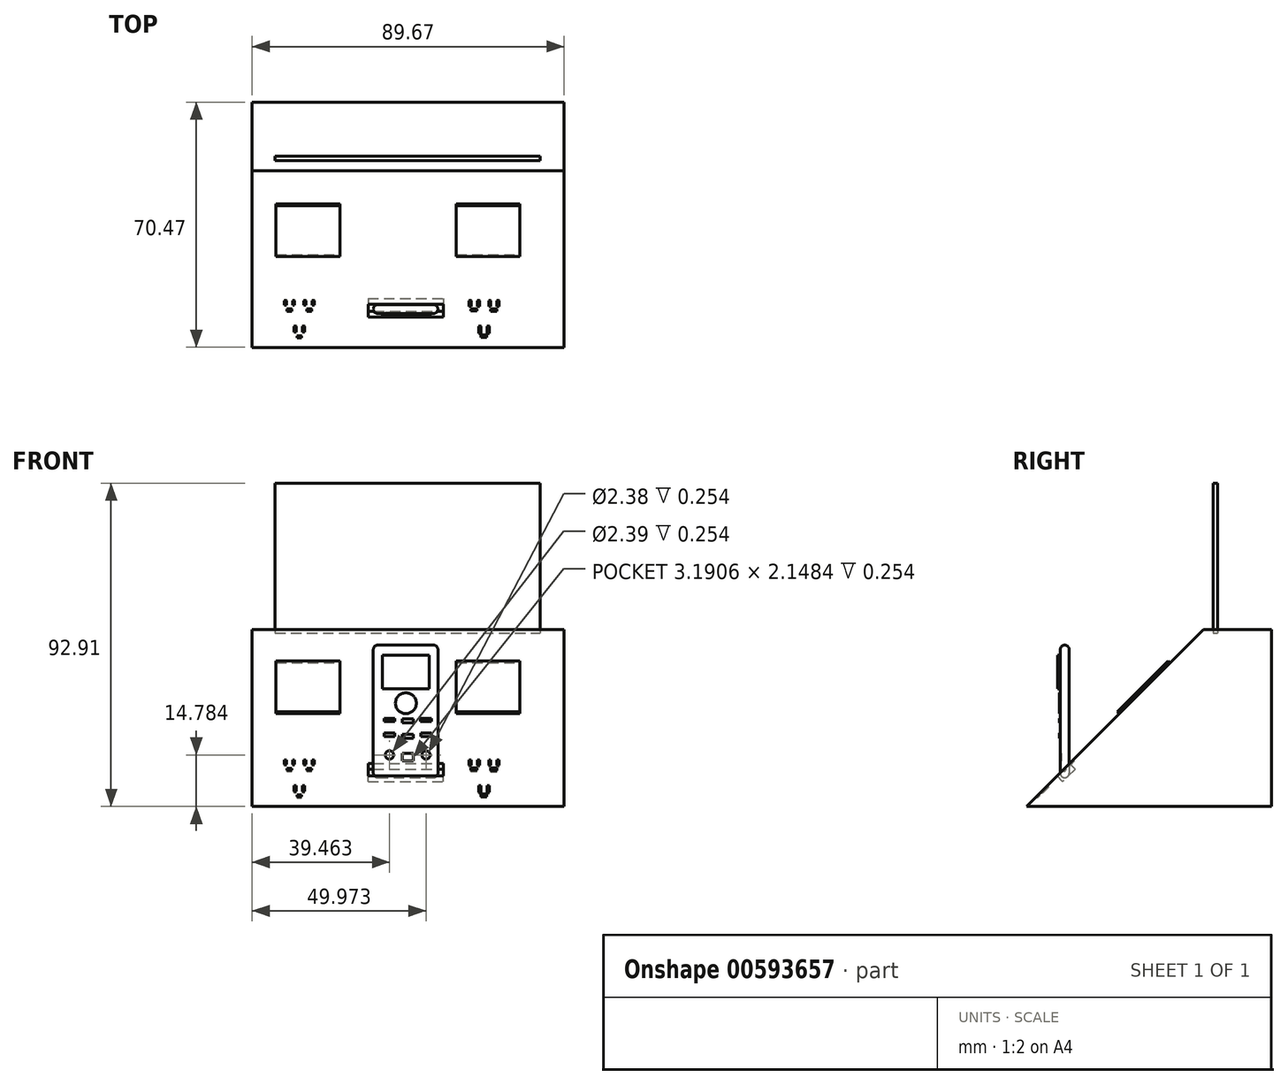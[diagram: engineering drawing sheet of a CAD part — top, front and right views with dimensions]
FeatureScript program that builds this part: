
annotation { "Feature Type Name" : "Feature", "Feature Type Description" : "" }
export const myFeature = defineFeature(function(context is Context, id is Id, definition is map)
    precondition{}
    {
        {
            var Q0;
            Q0=qCreatedBy(makeId("Top.planeOp"),FACE);
            var sketch = newSketch(context, id + "F0", { "sketchPlane" : qUnion([Q0])});
            skLineSegment(sketch, "E0.bottom", {"start": v(-44.91, 45.76) * mm, "end": v(44.76, 45.76) * mm});
            skLineSegment(sketch, "E0.top", {"start": v(-44.91, -37.41) * mm, "end": v(44.76, -37.41) * mm});
            skLineSegment(sketch, "E0.left", {"start": v(-44.91, 45.76) * mm, "end": v(-44.91, -37.41) * mm});
            skLineSegment(sketch, "E0.right", {"start": v(44.76, 45.76) * mm, "end": v(44.76, -37.41) * mm});
            skSolve(sketch);
        }
        {
            var Q0;
            Q0 = qSketchRegion(id + "F0", true);
            var Q1;
            Q1=makeQuery(id+"F0.imprint","IMPRINT",FACE,{"disambiguationData":[TD([[makeQuery(id+"F0.imprint","IMPRINT",EDGE,{"derivedFrom":sQuery(id+"F0.wireOp",EDGE,"E0.bottom")}),-1.0]])]});
            extrude(context, id + "F1", {"entities" : qUnion([Q0, Q1]), "depth" : 50.8 * mm, "offsetDistance" : 25.4 * mm});
        }
        {
            var Q0;
            Q0=makeQuery(id+"F1.opExtrude","CAP_EDGE",EDGE,{"disambiguationData":[OSD([sQuery(id+"F0.wireOp",EDGE,"E0.top")])],"isStart":false});
            chamfer(context, id + "F2", {"entities" : qUnion([Q0]), "width" : 63.5 * mm, "tangentPropagation" : true});
        }
        {
            var Q0;
            Q0=qCreatedBy(makeId("Front.planeOp"),FACE);
            var sketch = newSketch(context, id + "F3", { "sketchPlane" : qUnion([Q0])});
            skLineSegment(sketch, "E1.bottom", {"start": v(117.35, 33.47) * mm, "end": v(193.55, 33.47) * mm});
            skLineSegment(sketch, "E1.top", {"start": v(117.35, -9.66) * mm, "end": v(193.55, -9.66) * mm});
            skLineSegment(sketch, "E1.left", {"start": v(117.35, 33.47) * mm, "end": v(117.35, -9.66) * mm});
            skLineSegment(sketch, "E1.right", {"start": v(193.55, 33.47) * mm, "end": v(193.55, -9.66) * mm});
            skLineSegment(sketch, "E2.bottom", {"start": v(120.3, -7.68) * mm, "end": v(191.47, -7.68) * mm});
            skLineSegment(sketch, "E2.top", {"start": v(120.3, 31.24) * mm, "end": v(191.47, 31.24) * mm});
            skLineSegment(sketch, "E2.left", {"start": v(120.3, -7.68) * mm, "end": v(120.3, 31.24) * mm});
            skLineSegment(sketch, "E2.right", {"start": v(191.47, -7.68) * mm, "end": v(191.47, 31.24) * mm});
            skSolve(sketch);
        }
        {
            var Q0;
            Q0=makeQuery(id+"F3.imprint","IMPRINT",FACE,{"disambiguationData":[TD([[makeQuery(id+"F3.imprint","IMPRINT",EDGE,{"derivedFrom":sQuery(id+"F3.wireOp",EDGE,"E1.bottom")}),-1.0]])]});
            var Q1;
            Q1=makeQuery(id+"F3.imprint","IMPRINT",FACE,{"disambiguationData":[TD([[makeQuery(id+"F3.imprint","IMPRINT",EDGE,{"derivedFrom":sQuery(id+"F3.wireOp",EDGE,"E2.bottom")}),1.0]])]});
            extrude(context, id + "F4", {"entities" : qUnion([Q0, Q1]), "depth" : 1.27 * mm, "offsetDistance" : 25.4 * mm});
        }
        {
            var Q0;
            Q0=makeQuery(id+"F4.opExtrude","SWEPT_BODY",BODY,{"disambiguationData":[OSD([sQuery(id+"F3.wireOp",EDGE,"E1.bottom"),sQuery(id+"F3.wireOp",EDGE,"E1.top"),sQuery(id+"F3.wireOp",EDGE,"E1.left"),sQuery(id+"F3.wireOp",EDGE,"E1.right")])]});
            transform(context, id + "F5", {"entities" : qUnion([Q0]), "transformType" : TransformType.TRANSLATION_3D, "dx" : -155.7 * mm, "dy" : 30.23 * mm, "dz" : 59.44 * mm, "makeCopy" : false});
        }
        {
            var Q0;
            Q0=qCreatedBy(makeId("Front.planeOp"),FACE);
            var sketch = newSketch(context, id + "F6", { "sketchPlane" : qUnion([Q0])});
            skLineSegment(sketch, "E3.bottom", {"start": v(75.27, 43.86) * mm, "end": v(93.83, 43.86) * mm});
            skLineSegment(sketch, "E3.top", {"start": v(75.27, 5.76) * mm, "end": v(93.83, 5.76) * mm});
            skLineSegment(sketch, "E3.left", {"start": v(75.27, 43.86) * mm, "end": v(75.27, 5.76) * mm});
            skLineSegment(sketch, "E3.right", {"start": v(93.83, 43.86) * mm, "end": v(93.83, 5.76) * mm});
            skSolve(sketch);
        }
        {
            var Q0;
            Q0 = qSketchRegion(id + "F6", true);
            extrude(context, id + "F7", {"entities" : qUnion([Q0]), "depth" : 2.54 * mm, "offsetDistance" : 25.4 * mm});
        }
        {
            var Q0;
            Q0=makeQuery(id+"F7.opExtrude","CAP_EDGE",EDGE,{"disambiguationData":[OSD([sQuery(id+"F6.wireOp",EDGE,"E3.left")])],"isStart":true});
            var Q1;
            Q1=makeQuery(id+"F7.opExtrude","CAP_EDGE",EDGE,{"disambiguationData":[OSD([sQuery(id+"F6.wireOp",EDGE,"E3.left")])],"isStart":false});
            var Q2;
            Q2=makeQuery(id+"F7.opExtrude","CAP_EDGE",EDGE,{"disambiguationData":[OSD([sQuery(id+"F6.wireOp",EDGE,"E3.right")])],"isStart":true});
            var Q3;
            Q3=makeQuery(id+"F7.opExtrude","CAP_EDGE",EDGE,{"disambiguationData":[OSD([sQuery(id+"F6.wireOp",EDGE,"E3.right")])],"isStart":false});
            var Q4;
            Q4=makeQuery(id+"F7.opExtrude","SWEPT_FACE",FACE,{"disambiguationData":[OSD([sQuery(id+"F6.wireOp",EDGE,"E3.top")])]});
            var Q5;
            Q5=makeQuery(id+"F7.opExtrude","SWEPT_FACE",FACE,{"disambiguationData":[OSD([sQuery(id+"F6.wireOp",EDGE,"E3.bottom")])]});
            fillet(context, id + "F8", {"entities" : qUnion([Q0, Q1, Q2, Q3, Q4, Q5]), "radius" : 1.27 * mm, "tangentPropagation" : true, "allowEdgeOverflow" : false});
        }
        {
            var Q0;
            Q0=makeQuery(id+"F2.opChamfer","BLEND_FACE",FACE,{"disambiguationData":[OSD([sQuery(id+"F0.wireOp",EDGE,"E0.top")])]});
            var sketch = newSketch(context, id + "F9", { "sketchPlane" : qUnion([Q0])});
            skLineSegment(sketch, "E4.bottom", {"start": v(-11.58, 0) * mm, "end": v(10.01, 0) * mm});
            skLineSegment(sketch, "E4.left", {"start": v(-11.58, 0) * mm, "end": v(-11.58, 0) * mm});
            skLineSegment(sketch, "E4.right", {"start": v(10.01, 0) * mm, "end": v(10.01, 0) * mm});
            skLineSegment(sketch, "E5", {"start": v(-11.58, 0) * mm, "end": v(-11.58, -5.08) * mm});
            skLineSegment(sketch, "E6", {"start": v(-11.58, -5.08) * mm, "end": v(10.01, -5.08) * mm});
            skLineSegment(sketch, "E7", {"start": v(10.01, -5.08) * mm, "end": v(10.01, 0) * mm});
            skSolve(sketch);
        }
        {
            var Q0;
            Q0=makeQuery(id+"F9.imprint","IMPRINT",FACE,{"disambiguationData":[TD([[makeQuery(id+"F9.imprint","IMPRINT",EDGE,{"derivedFrom":sQuery(id+"F9.wireOp",EDGE,"E4.bottom")}),-1.0]])]});
            extrude(context, id + "F10", {"entities" : qUnion([Q0]), "operationType" : NewBodyOperationType.REMOVE, "oppositeDirection" : true, "depth" : 2.3 * mm, "offsetDistance" : 25.4 * mm});
        }
        {
            var Q0;
            Q0=makeQuery(id+"F7.opExtrude","SWEPT_BODY",BODY,{"disambiguationData":[OSD([sQuery(id+"F6.wireOp",EDGE,"E3.bottom"),sQuery(id+"F6.wireOp",EDGE,"E3.top"),sQuery(id+"F6.wireOp",EDGE,"E3.left"),sQuery(id+"F6.wireOp",EDGE,"E3.right")])]});
            transform(context, id + "F11", {"entities" : qUnion([Q0]), "transformType" : TransformType.TRANSLATION_3D, "dx" : -85.34 * mm, "dy" : -12.45 * mm, "dz" : 2.5 * mm, "makeCopy" : false});
        }
        {
            var Q0;
            Q0=makeQuery(id+"F7.opExtrude","CAP_FACE",FACE,{"disambiguationData":[OSD([sQuery(id+"F6.wireOp",EDGE,"E3.bottom"),sQuery(id+"F6.wireOp",EDGE,"E3.top"),sQuery(id+"F6.wireOp",EDGE,"E3.left"),sQuery(id+"F6.wireOp",EDGE,"E3.right")])],"isStart":false});
            var sketch = newSketch(context, id + "F12", { "sketchPlane" : qUnion([Q0])});
            skLineSegment(sketch, "E8.bottom", {"start": v(-7.42, 43.5) * mm, "end": v(5.98, 43.5) * mm});
            skLineSegment(sketch, "E8.top", {"start": v(-7.42, 33.79) * mm, "end": v(5.98, 33.79) * mm});
            skLineSegment(sketch, "E8.left", {"start": v(-7.42, 43.5) * mm, "end": v(-7.42, 33.79) * mm});
            skLineSegment(sketch, "E8.right", {"start": v(5.98, 43.5) * mm, "end": v(5.98, 33.79) * mm});
            skSolve(sketch);
        }
        {
            var Q0;
            Q0=makeQuery(id+"F12.imprint","IMPRINT",FACE,{"disambiguationData":[TD([[makeQuery(id+"F12.imprint","IMPRINT",EDGE,{"derivedFrom":sQuery(id+"F12.wireOp",EDGE,"E8.bottom")}),-1.0]])]});
            var Q1;
            Q1 = qSketchRegion(id + "F14", true);
            extrude(context, id + "F13", {"entities" : qUnion([Q0, Q1]), "operationType" : NewBodyOperationType.ADD, "depth" : 0.76 * mm, "offsetDistance" : 25.4 * mm});
        }
        {
            var Q0;
            Q0=makeQuery(id+"F7.opExtrude","CAP_FACE",FACE,{"disambiguationData":[OSD([sQuery(id+"F6.wireOp",EDGE,"E3.bottom"),sQuery(id+"F6.wireOp",EDGE,"E3.top"),sQuery(id+"F6.wireOp",EDGE,"E3.left"),sQuery(id+"F6.wireOp",EDGE,"E3.right")])],"isStart":false});
            var sketch = newSketch(context, id + "F14", { "sketchPlane" : qUnion([Q0])});
            skCircle(sketch, "E9", {"center": v(-0.72, 29.65) * mm, "radius": 3 * mm});
            skPoint(sketch, "E9.centerSnap0", {"position": v(-0.72, 33.79) * mm});
            skLineSegment(sketch, "E10.bottom", {"start": v(-7.02, 25.3) * mm, "end": v(-3.87, 25.3) * mm});
            skLineSegment(sketch, "E10.top", {"start": v(-7.02, 24.42) * mm, "end": v(-3.87, 24.42) * mm});
            skLineSegment(sketch, "E10.left", {"start": v(-7.02, 25.3) * mm, "end": v(-7.02, 24.42) * mm});
            skLineSegment(sketch, "E10.right", {"start": v(-3.87, 25.3) * mm, "end": v(-3.87, 24.42) * mm});
            skLineSegment(sketch, "E11.bottom", {"start": v(-1.77, 25.15) * mm, "end": v(1.39, 25.15) * mm});
            skLineSegment(sketch, "E11.top", {"start": v(-1.77, 23.99) * mm, "end": v(1.39, 23.99) * mm});
            skLineSegment(sketch, "E11.left", {"start": v(-1.77, 25.15) * mm, "end": v(-1.77, 23.99) * mm});
            skLineSegment(sketch, "E11.right", {"start": v(1.39, 25.15) * mm, "end": v(1.39, 23.99) * mm});
            skLineSegment(sketch, "E12.bottom", {"start": v(3.5, 25.3) * mm, "end": v(6.64, 25.3) * mm});
            skLineSegment(sketch, "E12.top", {"start": v(3.5, 24.42) * mm, "end": v(6.64, 24.42) * mm});
            skLineSegment(sketch, "E12.left", {"start": v(3.5, 25.3) * mm, "end": v(3.5, 24.42) * mm});
            skLineSegment(sketch, "E12.right", {"start": v(6.64, 25.3) * mm, "end": v(6.64, 24.42) * mm});
            skLineSegment(sketch, "E13.bottom", {"start": v(-7.02, 21.07) * mm, "end": v(-3.87, 21.07) * mm});
            skLineSegment(sketch, "E13.top", {"start": v(-7.02, 20.14) * mm, "end": v(-3.87, 20.14) * mm});
            skLineSegment(sketch, "E13.left", {"start": v(-7.02, 21.07) * mm, "end": v(-7.02, 20.14) * mm});
            skLineSegment(sketch, "E13.right", {"start": v(-3.87, 21.07) * mm, "end": v(-3.87, 20.14) * mm});
            skLineSegment(sketch, "E14.bottom", {"start": v(-1.77, 20.68) * mm, "end": v(1.39, 20.68) * mm});
            skLineSegment(sketch, "E14.top", {"start": v(-1.77, 19.54) * mm, "end": v(1.39, 19.54) * mm});
            skLineSegment(sketch, "E14.left", {"start": v(-1.77, 20.68) * mm, "end": v(-1.77, 19.54) * mm});
            skLineSegment(sketch, "E14.right", {"start": v(1.39, 20.68) * mm, "end": v(1.39, 19.54) * mm});
            skLineSegment(sketch, "E15.bottom", {"start": v(3.55, 21.07) * mm, "end": v(6.58, 21.07) * mm});
            skLineSegment(sketch, "E15.top", {"start": v(3.55, 20.14) * mm, "end": v(6.58, 20.14) * mm});
            skLineSegment(sketch, "E15.left", {"start": v(3.55, 21.07) * mm, "end": v(3.55, 20.14) * mm});
            skLineSegment(sketch, "E15.right", {"start": v(6.58, 21.07) * mm, "end": v(6.58, 20.14) * mm});
            skCircle(sketch, "E16", {"center": v(-5.45, 14.78) * mm, "radius": 1.2 * mm});
            skPoint(sketch, "E16.centerSnap0", {"position": v(-5.45, 20.14) * mm});
            skCircle(sketch, "E17", {"center": v(5.06, 14.78) * mm, "radius": 1.2 * mm});
            skPoint(sketch, "E17.centerSnap0", {"position": v(5.06, 20.14) * mm});
            skPoint(sketch, "E18.centerSnap0", {"position": v(-0.2, 19.54) * mm});
            skLineSegment(sketch, "E19.bottom", {"start": v(-1.77, 15.22) * mm, "end": v(1.42, 15.22) * mm});
            skLineSegment(sketch, "E19.top", {"start": v(-1.77, 13.07) * mm, "end": v(1.42, 13.07) * mm});
            skLineSegment(sketch, "E19.left", {"start": v(-1.77, 15.22) * mm, "end": v(-1.77, 13.07) * mm});
            skLineSegment(sketch, "E19.right", {"start": v(1.42, 15.22) * mm, "end": v(1.42, 13.07) * mm});
            skSolve(sketch);
        }
        {
            var Q0;
            Q0=makeQuery(id+"F14.imprint","IMPRINT",FACE,{"disambiguationData":[TD([[makeQuery(id+"F14.imprint","IMPRINT",EDGE,{"derivedFrom":sQuery(id+"F14.wireOp",EDGE,"E9")}),1.0]])]});
            var Q1;
            Q1=makeQuery(id+"F14.imprint","IMPRINT",FACE,{"disambiguationData":[TD([[makeQuery(id+"F14.imprint","IMPRINT",EDGE,{"derivedFrom":sQuery(id+"F14.wireOp",EDGE,"E10.bottom")}),-1.0]])]});
            var Q2;
            Q2=makeQuery(id+"F14.imprint","IMPRINT",FACE,{"disambiguationData":[TD([[makeQuery(id+"F14.imprint","IMPRINT",EDGE,{"derivedFrom":sQuery(id+"F14.wireOp",EDGE,"E11.bottom")}),-1.0]])]});
            var Q3;
            Q3=makeQuery(id+"F14.imprint","IMPRINT",FACE,{"disambiguationData":[TD([[makeQuery(id+"F14.imprint","IMPRINT",EDGE,{"derivedFrom":sQuery(id+"F14.wireOp",EDGE,"E12.bottom")}),-1.0]])]});
            var Q4;
            Q4=makeQuery(id+"F14.imprint","IMPRINT",FACE,{"disambiguationData":[TD([[makeQuery(id+"F14.imprint","IMPRINT",EDGE,{"derivedFrom":sQuery(id+"F14.wireOp",EDGE,"E13.bottom")}),-1.0]])]});
            var Q5;
            Q5=makeQuery(id+"F14.imprint","IMPRINT",FACE,{"disambiguationData":[TD([[makeQuery(id+"F14.imprint","IMPRINT",EDGE,{"derivedFrom":sQuery(id+"F14.wireOp",EDGE,"E14.bottom")}),-1.0]])]});
            var Q6;
            Q6=makeQuery(id+"F14.imprint","IMPRINT",FACE,{"disambiguationData":[TD([[makeQuery(id+"F14.imprint","IMPRINT",EDGE,{"derivedFrom":sQuery(id+"F14.wireOp",EDGE,"E15.bottom")}),-1.0]])]});
            extrude(context, id + "F15", {"entities" : qUnion([Q0, Q1, Q2, Q3, Q4, Q5, Q6]), "operationType" : NewBodyOperationType.ADD, "depth" : 0.25 * mm, "offsetDistance" : 25.4 * mm});
        }
        {
            var Q0;
            Q0=makeQuery(id+"F14.imprint","IMPRINT",FACE,{"disambiguationData":[TD([[makeQuery(id+"F14.imprint","IMPRINT",EDGE,{"derivedFrom":sQuery(id+"F14.wireOp",EDGE,"E16")}),1.0]])]});
            var Q1;
            Q1=makeQuery(id+"F14.imprint","IMPRINT",FACE,{"disambiguationData":[TD([[makeQuery(id+"F14.imprint","IMPRINT",EDGE,{"derivedFrom":sQuery(id+"F14.wireOp",EDGE,"E18")}),1.0]])]});
            var Q2;
            Q2=makeQuery(id+"F14.imprint","IMPRINT",FACE,{"disambiguationData":[TD([[makeQuery(id+"F14.imprint","IMPRINT",EDGE,{"derivedFrom":sQuery(id+"F14.wireOp",EDGE,"E17")}),1.0]])]});
            var Q3;
            Q3=makeQuery(id+"F14.imprint","IMPRINT",FACE,{"disambiguationData":[TD([[makeQuery(id+"F14.imprint","IMPRINT",EDGE,{"derivedFrom":sQuery(id+"F14.wireOp",EDGE,"E19.bottom")}),-1.0]])]});
            extrude(context, id + "F16", {"entities" : qUnion([Q0, Q1, Q2, Q3]), "operationType" : NewBodyOperationType.REMOVE, "oppositeDirection" : true, "depth" : 0.25 * mm, "offsetDistance" : 25.4 * mm});
        }
        {
            var Q0;
            Q0=makeQuery(id+"F2.opChamfer","BLEND_FACE",FACE,{"disambiguationData":[OSD([sQuery(id+"F0.wireOp",EDGE,"E0.top")])]});
            var sketch = newSketch(context, id + "F17", { "sketchPlane" : qUnion([Q0])});
            skLineSegment(sketch, "E20.bottom", {"start": v(-38.07, 40.86) * mm, "end": v(-19.71, 40.86) * mm});
            skLineSegment(sketch, "E20.top", {"start": v(-38.07, 20.24) * mm, "end": v(-19.71, 20.24) * mm});
            skLineSegment(sketch, "E20.left", {"start": v(-38.07, 40.86) * mm, "end": v(-38.07, 20.24) * mm});
            skLineSegment(sketch, "E20.right", {"start": v(-19.71, 40.86) * mm, "end": v(-19.71, 20.24) * mm});
            skLineSegment(sketch, "E21.bottom", {"start": v(13.74, 40.86) * mm, "end": v(32.09, 40.86) * mm});
            skLineSegment(sketch, "E21.top", {"start": v(13.74, 20.24) * mm, "end": v(32.09, 20.24) * mm});
            skLineSegment(sketch, "E21.left", {"start": v(13.74, 40.86) * mm, "end": v(13.74, 20.24) * mm});
            skLineSegment(sketch, "E21.right", {"start": v(32.09, 40.86) * mm, "end": v(32.09, 20.24) * mm});
            skSolve(sketch);
        }
        {
            var Q0;
            Q0=makeQuery(id+"F17.imprint","IMPRINT",FACE,{"disambiguationData":[TD([[makeQuery(id+"F17.imprint","IMPRINT",EDGE,{"derivedFrom":sQuery(id+"F17.wireOp",EDGE,"E20.bottom")}),-1.0]])]});
            var Q1;
            Q1=makeQuery(id+"F17.imprint","IMPRINT",FACE,{"disambiguationData":[TD([[makeQuery(id+"F17.imprint","IMPRINT",EDGE,{"derivedFrom":sQuery(id+"F17.wireOp",EDGE,"E21.bottom")}),-1.0]])]});
            extrude(context, id + "F18", {"entities" : qUnion([Q0, Q1]), "operationType" : NewBodyOperationType.ADD, "depth" : 0.76 * mm, "offsetDistance" : 25.4 * mm});
        }
        {
            var Q0;
            Q0=makeQuery(id+"F2.opChamfer","BLEND_FACE",FACE,{"disambiguationData":[OSD([sQuery(id+"F0.wireOp",EDGE,"E0.top")])]});
            var sketch = newSketch(context, id + "F19", { "sketchPlane" : qUnion([Q0])});
            skLineSegment(sketch, "E22.bottom", {"start": v(-36.96, 2.3) * mm, "end": v(-31.3, 2.3) * mm});
            skLineSegment(sketch, "E22.top", {"start": v(-36.96, -3.9) * mm, "end": v(-31.3, -3.9) * mm});
            skLineSegment(sketch, "E22.left", {"start": v(-36.96, 2.3) * mm, "end": v(-36.96, -3.9) * mm});
            skLineSegment(sketch, "E22.right", {"start": v(-31.3, 2.3) * mm, "end": v(-31.3, -3.9) * mm});
            skLineSegment(sketch, "E23.bottom", {"start": v(-31.3, 2.3) * mm, "end": v(-25.63, 2.3) * mm});
            skLineSegment(sketch, "E23.top", {"start": v(-31.3, -3.9) * mm, "end": v(-25.63, -3.9) * mm});
            skLineSegment(sketch, "E23.right", {"start": v(-25.63, 2.3) * mm, "end": v(-25.63, -3.9) * mm});
            skPoint(sketch, "E24.firstSnap0", {"position": v(-34.12, -3.9) * mm});
            skPoint(sketch, "E24.oppositeSnap0", {"position": v(-28.46, -3.9) * mm});
            skLineSegment(sketch, "E24.bottom", {"start": v(-34.12, -7.4) * mm, "end": v(-28.46, -7.4) * mm});
            skLineSegment(sketch, "E24.top", {"start": v(-34.12, -14.4) * mm, "end": v(-28.46, -14.4) * mm});
            skLineSegment(sketch, "E24.left", {"start": v(-34.12, -7.4) * mm, "end": v(-34.12, -14.4) * mm});
            skLineSegment(sketch, "E24.right", {"start": v(-28.46, -7.4) * mm, "end": v(-28.46, -14.4) * mm});
            skLineSegment(sketch, "E25.bottom", {"start": v(16.14, 2.3) * mm, "end": v(21.8, 2.3) * mm});
            skLineSegment(sketch, "E25.top", {"start": v(16.14, -3.9) * mm, "end": v(21.8, -3.9) * mm});
            skLineSegment(sketch, "E25.left", {"start": v(16.14, 2.3) * mm, "end": v(16.14, -3.9) * mm});
            skLineSegment(sketch, "E25.right", {"start": v(21.8, 2.3) * mm, "end": v(21.8, -3.9) * mm});
            skLineSegment(sketch, "E26.bottom", {"start": v(21.8, 2.3) * mm, "end": v(27.46, 2.3) * mm});
            skLineSegment(sketch, "E26.top", {"start": v(21.8, -3.9) * mm, "end": v(27.46, -3.9) * mm});
            skLineSegment(sketch, "E26.right", {"start": v(27.46, 2.3) * mm, "end": v(27.46, -3.9) * mm});
            skPoint(sketch, "E27.firstSnap0", {"position": v(18.97, -3.9) * mm});
            skPoint(sketch, "E27.oppositeSnap0", {"position": v(24.63, -3.9) * mm});
            skLineSegment(sketch, "E27.bottom", {"start": v(18.97, -7.74) * mm, "end": v(24.63, -7.74) * mm});
            skLineSegment(sketch, "E27.top", {"start": v(18.97, -14.4) * mm, "end": v(24.63, -14.4) * mm});
            skLineSegment(sketch, "E27.left", {"start": v(18.97, -7.74) * mm, "end": v(18.97, -14.4) * mm});
            skLineSegment(sketch, "E27.right", {"start": v(24.63, -7.74) * mm, "end": v(24.63, -14.4) * mm});
            skLineSegment(sketch, "E28.bottom", {"start": v(-35.69, 1.48) * mm, "end": v(-35.06, 1.48) * mm});
            skLineSegment(sketch, "E28.top", {"start": v(-35.69, -0.36) * mm, "end": v(-35.06, -0.36) * mm});
            skLineSegment(sketch, "E28.left", {"start": v(-35.69, 1.48) * mm, "end": v(-35.69, -0.36) * mm});
            skLineSegment(sketch, "E28.right", {"start": v(-35.06, 1.48) * mm, "end": v(-35.06, -0.36) * mm});
            skLineSegment(sketch, "E29.bottom", {"start": v(-33.31, 1.48) * mm, "end": v(-32.75, 1.48) * mm});
            skLineSegment(sketch, "E29.top", {"start": v(-33.31, -0.36) * mm, "end": v(-32.75, -0.36) * mm});
            skLineSegment(sketch, "E29.left", {"start": v(-33.31, 1.48) * mm, "end": v(-33.31, -0.36) * mm});
            skLineSegment(sketch, "E29.right", {"start": v(-32.75, 1.48) * mm, "end": v(-32.75, -0.36) * mm});
            skLineSegment(sketch, "E30.bottom", {"start": v(-30.02, 1.48) * mm, "end": v(-29.39, 1.48) * mm});
            skLineSegment(sketch, "E30.top", {"start": v(-30.02, -0.36) * mm, "end": v(-29.39, -0.36) * mm});
            skLineSegment(sketch, "E30.left", {"start": v(-30.02, 1.48) * mm, "end": v(-30.02, -0.36) * mm});
            skLineSegment(sketch, "E30.right", {"start": v(-29.39, 1.48) * mm, "end": v(-29.39, -0.36) * mm});
            skLineSegment(sketch, "E31.bottom", {"start": v(-27.63, 1.48) * mm, "end": v(-27, 1.48) * mm});
            skLineSegment(sketch, "E31.top", {"start": v(-27.63, -0.36) * mm, "end": v(-27, -0.36) * mm});
            skLineSegment(sketch, "E31.left", {"start": v(-27.63, 1.48) * mm, "end": v(-27.63, -0.36) * mm});
            skLineSegment(sketch, "E31.right", {"start": v(-27, 1.48) * mm, "end": v(-27, -0.36) * mm});
            skLineSegment(sketch, "E32.bottom", {"start": v(-32.85, -8.98) * mm, "end": v(-32.22, -8.98) * mm});
            skLineSegment(sketch, "E32.top", {"start": v(-32.85, -11.3) * mm, "end": v(-32.22, -11.3) * mm});
            skLineSegment(sketch, "E32.left", {"start": v(-32.85, -8.98) * mm, "end": v(-32.85, -11.3) * mm});
            skLineSegment(sketch, "E32.right", {"start": v(-32.22, -8.98) * mm, "end": v(-32.22, -11.3) * mm});
            skLineSegment(sketch, "E33.bottom", {"start": v(-30.47, -8.98) * mm, "end": v(-29.83, -8.98) * mm});
            skLineSegment(sketch, "E33.top", {"start": v(-30.47, -11.3) * mm, "end": v(-29.83, -11.3) * mm});
            skLineSegment(sketch, "E33.left", {"start": v(-30.47, -8.98) * mm, "end": v(-30.47, -11.3) * mm});
            skLineSegment(sketch, "E33.right", {"start": v(-29.83, -8.98) * mm, "end": v(-29.83, -11.3) * mm});
            skLineSegment(sketch, "E34.bottom", {"start": v(-34.88, -1.96) * mm, "end": v(-33.52, -1.96) * mm});
            skLineSegment(sketch, "E34.top", {"start": v(-34.88, -2.77) * mm, "end": v(-33.52, -2.77) * mm});
            skLineSegment(sketch, "E34.left", {"start": v(-34.88, -1.96) * mm, "end": v(-34.88, -2.77) * mm});
            skLineSegment(sketch, "E34.right", {"start": v(-33.52, -1.96) * mm, "end": v(-33.52, -2.77) * mm});
            skLineSegment(sketch, "E35.bottom", {"start": v(-29.15, -1.96) * mm, "end": v(-27.84, -1.96) * mm});
            skLineSegment(sketch, "E35.top", {"start": v(-29.15, -2.77) * mm, "end": v(-27.84, -2.77) * mm});
            skLineSegment(sketch, "E35.left", {"start": v(-29.15, -1.96) * mm, "end": v(-29.15, -2.77) * mm});
            skLineSegment(sketch, "E35.right", {"start": v(-27.84, -1.96) * mm, "end": v(-27.84, -2.77) * mm});
            skLineSegment(sketch, "E36.bottom", {"start": v(-32.03, -12.85) * mm, "end": v(-30.67, -12.85) * mm});
            skLineSegment(sketch, "E36.top", {"start": v(-32.03, -13.54) * mm, "end": v(-30.67, -13.54) * mm});
            skLineSegment(sketch, "E36.left", {"start": v(-32.03, -12.85) * mm, "end": v(-32.03, -13.54) * mm});
            skLineSegment(sketch, "E36.right", {"start": v(-30.67, -12.85) * mm, "end": v(-30.67, -13.54) * mm});
            skPoint(sketch, "E37.oppositeSnap0", {"position": v(16.14, -0.8) * mm});
            skLineSegment(sketch, "E37.bottom", {"start": v(17.4, 1.48) * mm, "end": v(18.04, 1.48) * mm});
            skLineSegment(sketch, "E37.top", {"start": v(17.4, -0.8) * mm, "end": v(18.04, -0.8) * mm});
            skLineSegment(sketch, "E37.left", {"start": v(17.4, 1.48) * mm, "end": v(17.4, -0.8) * mm});
            skLineSegment(sketch, "E37.right", {"start": v(18.04, 1.48) * mm, "end": v(18.04, -0.8) * mm});
            skLineSegment(sketch, "E38.bottom", {"start": v(19.8, 1.48) * mm, "end": v(20.43, 1.48) * mm});
            skLineSegment(sketch, "E38.top", {"start": v(19.8, -0.8) * mm, "end": v(20.43, -0.8) * mm});
            skLineSegment(sketch, "E38.left", {"start": v(19.8, 1.48) * mm, "end": v(19.8, -0.8) * mm});
            skLineSegment(sketch, "E38.right", {"start": v(20.43, 1.48) * mm, "end": v(20.43, -0.8) * mm});
            skLineSegment(sketch, "E39.bottom", {"start": v(23.07, 1.48) * mm, "end": v(23.7, 1.48) * mm});
            skLineSegment(sketch, "E39.top", {"start": v(23.07, -0.8) * mm, "end": v(23.7, -0.8) * mm});
            skLineSegment(sketch, "E39.left", {"start": v(23.07, 1.48) * mm, "end": v(23.07, -0.8) * mm});
            skLineSegment(sketch, "E39.right", {"start": v(23.7, 1.48) * mm, "end": v(23.7, -0.8) * mm});
            skLineSegment(sketch, "E40.bottom", {"start": v(25.46, 1.48) * mm, "end": v(26.1, 1.48) * mm});
            skLineSegment(sketch, "E40.top", {"start": v(25.46, -0.8) * mm, "end": v(26.1, -0.8) * mm});
            skLineSegment(sketch, "E40.left", {"start": v(25.46, 1.48) * mm, "end": v(25.46, -0.8) * mm});
            skLineSegment(sketch, "E40.right", {"start": v(26.1, 1.48) * mm, "end": v(26.1, -0.8) * mm});
            skLineSegment(sketch, "E41.bottom", {"start": v(22.62, -8.98) * mm, "end": v(23.26, -8.98) * mm});
            skLineSegment(sketch, "E41.top", {"start": v(22.62, -11.74) * mm, "end": v(23.26, -11.74) * mm});
            skLineSegment(sketch, "E41.left", {"start": v(22.62, -8.98) * mm, "end": v(22.62, -11.74) * mm});
            skLineSegment(sketch, "E41.right", {"start": v(23.26, -8.98) * mm, "end": v(23.26, -11.74) * mm});
            skLineSegment(sketch, "E42.bottom", {"start": v(20.24, -8.98) * mm, "end": v(20.87, -8.98) * mm});
            skLineSegment(sketch, "E42.top", {"start": v(20.24, -11.74) * mm, "end": v(20.87, -11.74) * mm});
            skLineSegment(sketch, "E42.left", {"start": v(20.24, -8.98) * mm, "end": v(20.24, -11.74) * mm});
            skLineSegment(sketch, "E42.right", {"start": v(20.87, -8.98) * mm, "end": v(20.87, -11.74) * mm});
            skLineSegment(sketch, "E43.bottom", {"start": v(17.97, -1.87) * mm, "end": v(19.74, -1.87) * mm});
            skLineSegment(sketch, "E43.top", {"start": v(17.97, -2.73) * mm, "end": v(19.74, -2.73) * mm});
            skLineSegment(sketch, "E43.left", {"start": v(17.97, -1.87) * mm, "end": v(17.97, -2.73) * mm});
            skLineSegment(sketch, "E43.right", {"start": v(19.74, -1.87) * mm, "end": v(19.74, -2.73) * mm});
            skLineSegment(sketch, "E44.bottom", {"start": v(23.7, -1.9) * mm, "end": v(25.44, -1.9) * mm});
            skLineSegment(sketch, "E44.top", {"start": v(23.7, -2.88) * mm, "end": v(25.44, -2.88) * mm});
            skLineSegment(sketch, "E44.left", {"start": v(23.7, -1.9) * mm, "end": v(23.7, -2.88) * mm});
            skLineSegment(sketch, "E44.right", {"start": v(25.44, -1.9) * mm, "end": v(25.44, -2.88) * mm});
            skLineSegment(sketch, "E45.bottom", {"start": v(20.86, -12.47) * mm, "end": v(22.5, -12.47) * mm});
            skLineSegment(sketch, "E45.top", {"start": v(20.86, -13.42) * mm, "end": v(22.5, -13.42) * mm});
            skLineSegment(sketch, "E45.left", {"start": v(20.86, -12.47) * mm, "end": v(20.86, -13.42) * mm});
            skLineSegment(sketch, "E45.right", {"start": v(22.5, -12.47) * mm, "end": v(22.5, -13.42) * mm});
            skSolve(sketch);
        }
        {
            var Q0;
            Q0=makeQuery(id+"F19.imprint","IMPRINT",FACE,{"disambiguationData":[TD([[makeQuery(id+"F19.imprint","IMPRINT",EDGE,{"derivedFrom":sQuery(id+"F19.wireOp",EDGE,"E28.bottom")}),-1.0]])]});
            var Q1;
            Q1=makeQuery(id+"F19.imprint","IMPRINT",FACE,{"disambiguationData":[TD([[makeQuery(id+"F19.imprint","IMPRINT",EDGE,{"derivedFrom":sQuery(id+"F19.wireOp",EDGE,"E34.bottom")}),-1.0]])]});
            var Q2;
            Q2=makeQuery(id+"F19.imprint","IMPRINT",FACE,{"disambiguationData":[TD([[makeQuery(id+"F19.imprint","IMPRINT",EDGE,{"derivedFrom":sQuery(id+"F19.wireOp",EDGE,"E29.bottom")}),-1.0]])]});
            var Q3;
            Q3=makeQuery(id+"F19.imprint","IMPRINT",FACE,{"disambiguationData":[TD([[makeQuery(id+"F19.imprint","IMPRINT",EDGE,{"derivedFrom":sQuery(id+"F19.wireOp",EDGE,"E30.bottom")}),-1.0]])]});
            var Q4;
            Q4=makeQuery(id+"F19.imprint","IMPRINT",FACE,{"disambiguationData":[TD([[makeQuery(id+"F19.imprint","IMPRINT",EDGE,{"derivedFrom":sQuery(id+"F19.wireOp",EDGE,"E35.bottom")}),-1.0]])]});
            var Q5;
            Q5=makeQuery(id+"F19.imprint","IMPRINT",FACE,{"disambiguationData":[TD([[makeQuery(id+"F19.imprint","IMPRINT",EDGE,{"derivedFrom":sQuery(id+"F19.wireOp",EDGE,"E31.bottom")}),-1.0]])]});
            var Q6;
            Q6=makeQuery(id+"F19.imprint","IMPRINT",FACE,{"disambiguationData":[TD([[makeQuery(id+"F19.imprint","IMPRINT",EDGE,{"derivedFrom":sQuery(id+"F19.wireOp",EDGE,"E32.bottom")}),-1.0]])]});
            var Q7;
            Q7=makeQuery(id+"F19.imprint","IMPRINT",FACE,{"disambiguationData":[TD([[makeQuery(id+"F19.imprint","IMPRINT",EDGE,{"derivedFrom":sQuery(id+"F19.wireOp",EDGE,"E33.bottom")}),-1.0]])]});
            var Q8;
            Q8=makeQuery(id+"F19.imprint","IMPRINT",FACE,{"disambiguationData":[TD([[makeQuery(id+"F19.imprint","IMPRINT",EDGE,{"derivedFrom":sQuery(id+"F19.wireOp",EDGE,"E36.bottom")}),-1.0]])]});
            var Q9;
            Q9=makeQuery(id+"F19.imprint","IMPRINT",FACE,{"disambiguationData":[TD([[makeQuery(id+"F19.imprint","IMPRINT",EDGE,{"derivedFrom":sQuery(id+"F19.wireOp",EDGE,"E43.bottom")}),-1.0]])]});
            var Q10;
            Q10=makeQuery(id+"F19.imprint","IMPRINT",FACE,{"disambiguationData":[TD([[makeQuery(id+"F19.imprint","IMPRINT",EDGE,{"derivedFrom":sQuery(id+"F19.wireOp",EDGE,"E44.bottom")}),-1.0]])]});
            var Q11;
            Q11=makeQuery(id+"F19.imprint","IMPRINT",FACE,{"disambiguationData":[TD([[makeQuery(id+"F19.imprint","IMPRINT",EDGE,{"derivedFrom":sQuery(id+"F19.wireOp",EDGE,"E45.bottom")}),-1.0]])]});
            var Q12;
            Q12=makeQuery(id+"F19.imprint","IMPRINT",FACE,{"disambiguationData":[TD([[makeQuery(id+"F19.imprint","IMPRINT",EDGE,{"derivedFrom":sQuery(id+"F19.wireOp",EDGE,"E42.bottom")}),-1.0]])]});
            var Q13;
            Q13=makeQuery(id+"F19.imprint","IMPRINT",FACE,{"disambiguationData":[TD([[makeQuery(id+"F19.imprint","IMPRINT",EDGE,{"derivedFrom":sQuery(id+"F19.wireOp",EDGE,"E39.bottom")}),-1.0]])]});
            var Q14;
            Q14=makeQuery(id+"F19.imprint","IMPRINT",FACE,{"disambiguationData":[TD([[makeQuery(id+"F19.imprint","IMPRINT",EDGE,{"derivedFrom":sQuery(id+"F19.wireOp",EDGE,"E40.bottom")}),-1.0]])]});
            var Q15;
            Q15=makeQuery(id+"F19.imprint","IMPRINT",FACE,{"disambiguationData":[TD([[makeQuery(id+"F19.imprint","IMPRINT",EDGE,{"derivedFrom":sQuery(id+"F19.wireOp",EDGE,"E38.bottom")}),-1.0]])]});
            var Q16;
            Q16=makeQuery(id+"F19.imprint","IMPRINT",FACE,{"disambiguationData":[TD([[makeQuery(id+"F19.imprint","IMPRINT",EDGE,{"derivedFrom":sQuery(id+"F19.wireOp",EDGE,"E37.bottom")}),-1.0]])]});
            var Q17;
            Q17=makeQuery(id+"F19.imprint","IMPRINT",FACE,{"disambiguationData":[TD([[makeQuery(id+"F19.imprint","IMPRINT",EDGE,{"derivedFrom":sQuery(id+"F19.wireOp",EDGE,"E41.bottom")}),-1.0]])]});
            extrude(context, id + "F20", {"entities" : qUnion([Q0, Q1, Q2, Q3, Q4, Q5, Q6, Q7, Q8, Q9, Q10, Q11, Q12, Q13, Q14, Q15, Q16, Q17]), "operationType" : NewBodyOperationType.REMOVE, "oppositeDirection" : true, "depth" : 0.5 * mm, "offsetDistance" : 25.4 * mm});
        }
    });
